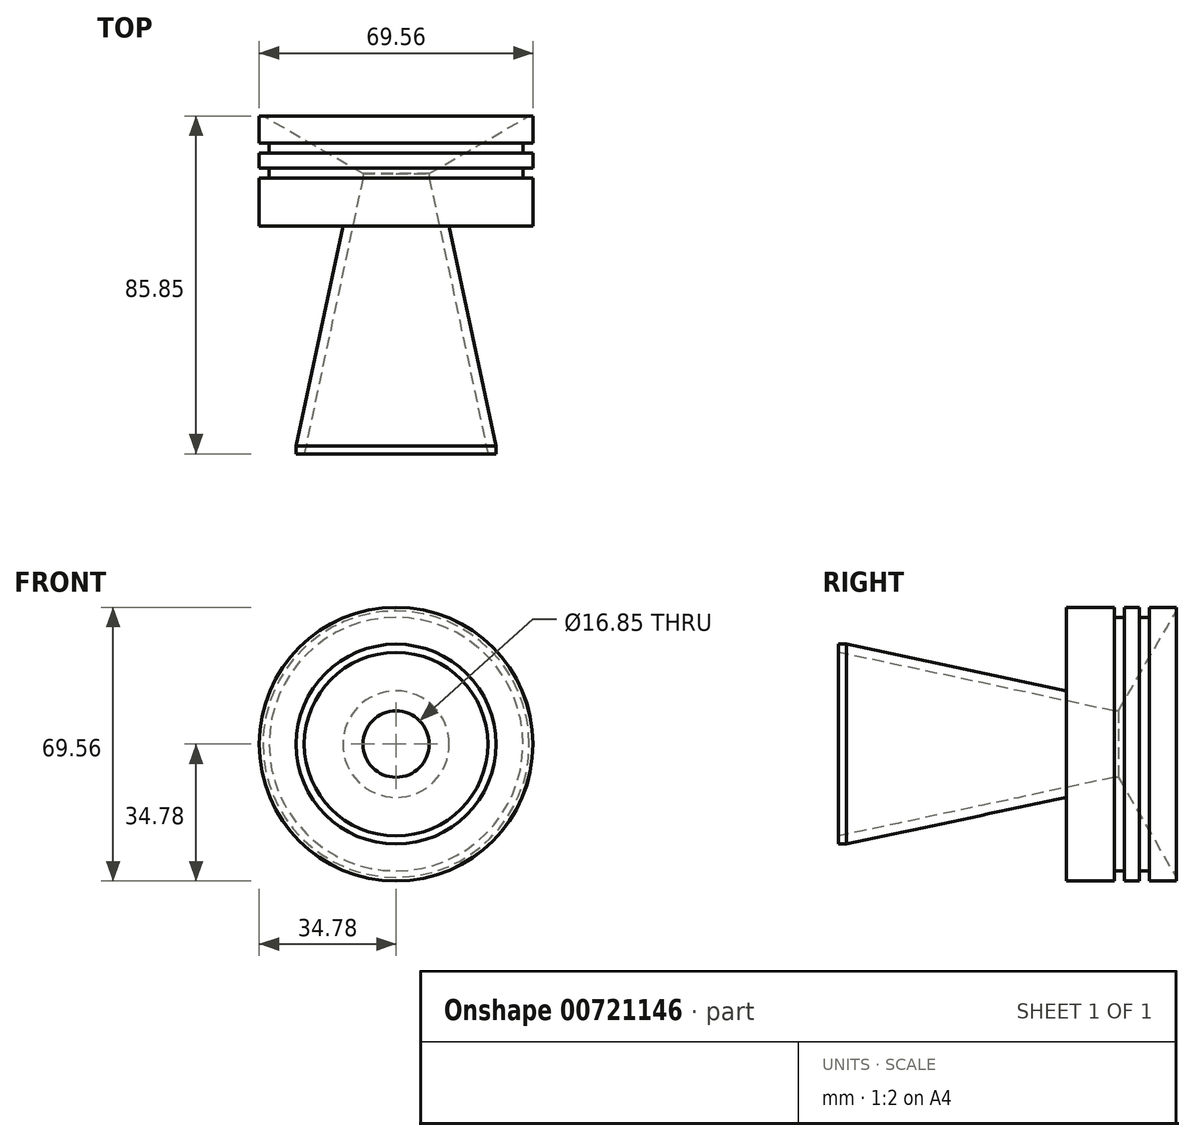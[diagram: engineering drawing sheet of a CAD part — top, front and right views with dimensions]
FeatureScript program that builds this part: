
annotation { "Feature Type Name" : "Feature", "Feature Type Description" : "" }
export const myFeature = defineFeature(function(context is Context, id is Id, definition is map)
    precondition{}
    {
        {
            var Q0;
            Q0=qCreatedBy(makeId("Front.planeOp"),FACE);
            var sketch = newSketch(context, id + "F0", { "sketchPlane" : qUnion([Q0])});
            skCircle(sketch, "E0", {"center": v(0, 0) * mm, "radius": 25.4 * mm});
            skCircle(sketch, "E1", {"center": v(0, 0) * mm, "radius": 7.94 * mm});
            skSolve(sketch);
        }
        {
            var Q0;
            Q0=makeQuery(id+"F0.imprint","IMPRINT",FACE,{"disambiguationData":[TD([[makeQuery(id+"F0.imprint","IMPRINT",EDGE,{"derivedFrom":sQuery(id+"F0.wireOp",EDGE,"E0")}),1.0]])]});
            extrude(context, id + "F1", {"entities" : qUnion([Q0]), "depth" : 57.9 * mm, "offsetDistance" : 25.4 * mm});
        }
        {
            var Q0;
            Q0=makeQuery(id+"F1.opExtrude","CAP_EDGE",EDGE,{"disambiguationData":[OSD([sQuery(id+"F0.wireOp",EDGE,"E0")])],"isStart":true});
            chamfer(context, id + "F2", {"entities" : qUnion([Q0]), "chamferType" : ChamferType.OFFSET_ANGLE, "width" : 55.88 * mm, "oppositeDirection" : false, "angle" : 12 * degree, "tangentPropagation" : true});
        }
        {
            var Q0;
            Q0=makeQuery(id+"F1.opExtrude","CAP_FACE",FACE,{"disambiguationData":[OSD([sQuery(id+"F0.wireOp",EDGE,"E0"),sQuery(id+"F0.wireOp",EDGE,"E1")])],"isStart":true});
            var sketch = newSketch(context, id + "F3", { "sketchPlane" : qUnion([Q0])});
            skCircle(sketch, "E2", {"center": v(0, 0) * mm, "radius": 34.76 * mm});
            skSolve(sketch);
        }
        {
            var Q0;
            Q0=makeQuery(id+"F3.imprint","IMPRINT",FACE,{"disambiguationData":[TD([[makeQuery(id+"F3.imprint","IMPRINT",EDGE,{"derivedFrom":sQuery(id+"F3.wireOp",EDGE,"E2")}),1.0]])]});
            var Q1;
            {var subQ0=sQuery(id+"F0.wireOp",EDGE,"E1");Q1=makeQuery(id+"F3.imprint","IMPRINT",FACE,{"disambiguationData":[TD([[makeQuery(id+"F3.imprint","IMPRINT",EDGE,{"derivedFrom":makeQuery(id+"F1.opExtrude","CAP_EDGE",EDGE,{"disambiguationData":[OSD([subQ0])],"isStart":true})}),1.0]])]});}
            extrude(context, id + "F4", {"entities" : qUnion([Q0, Q1]), "operationType" : NewBodyOperationType.ADD, "depth" : 12.2 * mm, "offsetDistance" : 25.4 * mm});
        }
        {
            var Q0;
            Q0=makeQuery(id+"F1.opExtrude","CAP_EDGE",EDGE,{"disambiguationData":[OSD([sQuery(id+"F0.wireOp",EDGE,"E1")])],"isStart":false});
            chamfer(context, id + "F5", {"entities" : qUnion([Q0]), "chamferType" : ChamferType.OFFSET_ANGLE, "width" : 72.39 * mm, "oppositeDirection" : false, "angle" : 12 * degree, "tangentPropagation" : true});
        }
        {
            var Q0;
            Q0=makeQuery(id+"F4.opExtrude","CAP_FACE",FACE,{"disambiguationData":[OSD([sQuery(id+"F0.wireOp",EDGE,"E1"),sQuery(id+"F3.wireOp",EDGE,"E2")])],"isStart":false});
            var sketch = newSketch(context, id + "F6", { "sketchPlane" : qUnion([Q0])});
            skCircle(sketch, "E3", {"center": v(0, 0) * mm, "radius": 32.22 * mm});
            skSolve(sketch);
        }
        {
            var Q0;
            Q0=makeQuery(id+"F6.imprint","IMPRINT",FACE,{"disambiguationData":[TD([[makeQuery(id+"F6.imprint","IMPRINT",EDGE,{"derivedFrom":sQuery(id+"F6.wireOp",EDGE,"E3")}),1.0]])]});
            extrude(context, id + "F7", {"entities" : qUnion([Q0]), "operationType" : NewBodyOperationType.ADD, "depth" : 2.54 * mm, "offsetDistance" : 25.4 * mm});
        }
        {
            var Q0;
            Q0=makeQuery(id+"F7.opExtrude","CAP_FACE",FACE,{"disambiguationData":[OSD([sQuery(id+"F0.wireOp",EDGE,"E1"),sQuery(id+"F3.wireOp",EDGE,"E2"),sQuery(id+"F6.wireOp",EDGE,"E3")])],"isStart":false});
            var sketch = newSketch(context, id + "F8", { "sketchPlane" : qUnion([Q0])});
            skCircle(sketch, "E4", {"center": v(0, 0) * mm, "radius": 34.78 * mm});
            skSolve(sketch);
        }
        {
            var Q0;
            Q0=makeQuery(id+"F8.imprint","IMPRINT",FACE,{"disambiguationData":[TD([[makeQuery(id+"F8.imprint","IMPRINT",EDGE,{"derivedFrom":sQuery(id+"F8.wireOp",EDGE,"E4")}),1.0]])]});
            var Q1;
            Q1=makeQuery(id+"F8.imprint","IMPRINT",FACE,{"disambiguationData":[TD([[makeQuery(id+"F8.imprint","IMPRINT",EDGE,{"derivedFrom":makeQuery(id+"F7.opExtrude","CAP_EDGE",EDGE,{"disambiguationData":[OSD([sQuery(id+"F6.wireOp",EDGE,"E3")])],"isStart":false})}),1.0]])]});
            extrude(context, id + "F9", {"entities" : qUnion([Q0, Q1]), "operationType" : NewBodyOperationType.ADD, "depth" : 3.8 * mm, "offsetDistance" : 25.4 * mm});
        }
        {
            var Q0;
            Q0=makeQuery(id+"F9.opExtrude","CAP_FACE",FACE,{"disambiguationData":[OSD([sQuery(id+"F0.wireOp",EDGE,"E1"),sQuery(id+"F3.wireOp",EDGE,"E2"),sQuery(id+"F8.wireOp",EDGE,"E4")])],"isStart":false});
            var sketch = newSketch(context, id + "F10", { "sketchPlane" : qUnion([Q0])});
            skCircle(sketch, "E5", {"center": v(0, 0) * mm, "radius": 32.22 * mm});
            skSolve(sketch);
        }
        {
            var Q0;
            Q0=makeQuery(id+"F10.imprint","IMPRINT",FACE,{"disambiguationData":[TD([[makeQuery(id+"F10.imprint","IMPRINT",EDGE,{"derivedFrom":sQuery(id+"F10.wireOp",EDGE,"E5")}),1.0]])]});
            extrude(context, id + "F11", {"entities" : qUnion([Q0]), "operationType" : NewBodyOperationType.ADD, "depth" : 2.54 * mm, "offsetDistance" : 25.4 * mm});
        }
        {
            var Q0;
            Q0=makeQuery(id+"F11.opExtrude","CAP_FACE",FACE,{"disambiguationData":[OSD([sQuery(id+"F0.wireOp",EDGE,"E1"),sQuery(id+"F3.wireOp",EDGE,"E2"),sQuery(id+"F10.wireOp",EDGE,"E5")])],"isStart":false});
            var sketch = newSketch(context, id + "F12", { "sketchPlane" : qUnion([Q0])});
            skSolve(sketch);
        }
        {
            var Q0;
            Q0=makeQuery(id+"F12.imprint","IMPRINT",FACE,{"disambiguationData":[TD([[makeQuery(id+"F12.imprint","IMPRINT",EDGE,{"derivedFrom":makeQuery(id+"F11.opExtrude","CAP_EDGE",EDGE,{"disambiguationData":[OSD([sQuery(id+"F10.wireOp",EDGE,"E5")])],"isStart":false})}),1.0]])]});
            var sketch = newSketch(context, id + "F13", { "sketchPlane" : qUnion([Q0])});
            skCircle(sketch, "E6", {"center": v(0, 0) * mm, "radius": 34.76 * mm});
            skSolve(sketch);
        }
        {
            var Q0;
            Q0=makeQuery(id+"F13.imprint","IMPRINT",FACE,{"disambiguationData":[TD([[makeQuery(id+"F13.imprint","IMPRINT",EDGE,{"derivedFrom":sQuery(id+"F13.wireOp",EDGE,"E6")}),1.0]])]});
            var Q1;
            Q1=makeQuery(id+"F12.imprint","IMPRINT",FACE,{"disambiguationData":[TD([[makeQuery(id+"F12.imprint","IMPRINT",EDGE,{"derivedFrom":makeQuery(id+"F11.opExtrude","CAP_EDGE",EDGE,{"disambiguationData":[OSD([sQuery(id+"F10.wireOp",EDGE,"E5")])],"isStart":false})}),1.0]])]});
            extrude(context, id + "F14", {"entities" : qUnion([Q0, Q1]), "operationType" : NewBodyOperationType.ADD, "depth" : 6.86 * mm, "offsetDistance" : 25.4 * mm});
        }
        {
            var Q0;
            Q0=makeQuery(id+"F14.opExtrude","CAP_EDGE",EDGE,{"disambiguationData":[OSD([sQuery(id+"F0.wireOp",EDGE,"E1"),sQuery(id+"F3.wireOp",EDGE,"E2")])],"isStart":false});
            chamfer(context, id + "F15", {"entities" : qUnion([Q0]), "chamferType" : ChamferType.OFFSET_ANGLE, "width" : 25.4 * mm, "oppositeDirection" : false, "angle" : 30 * degree, "tangentPropagation" : true});
        }
    });
